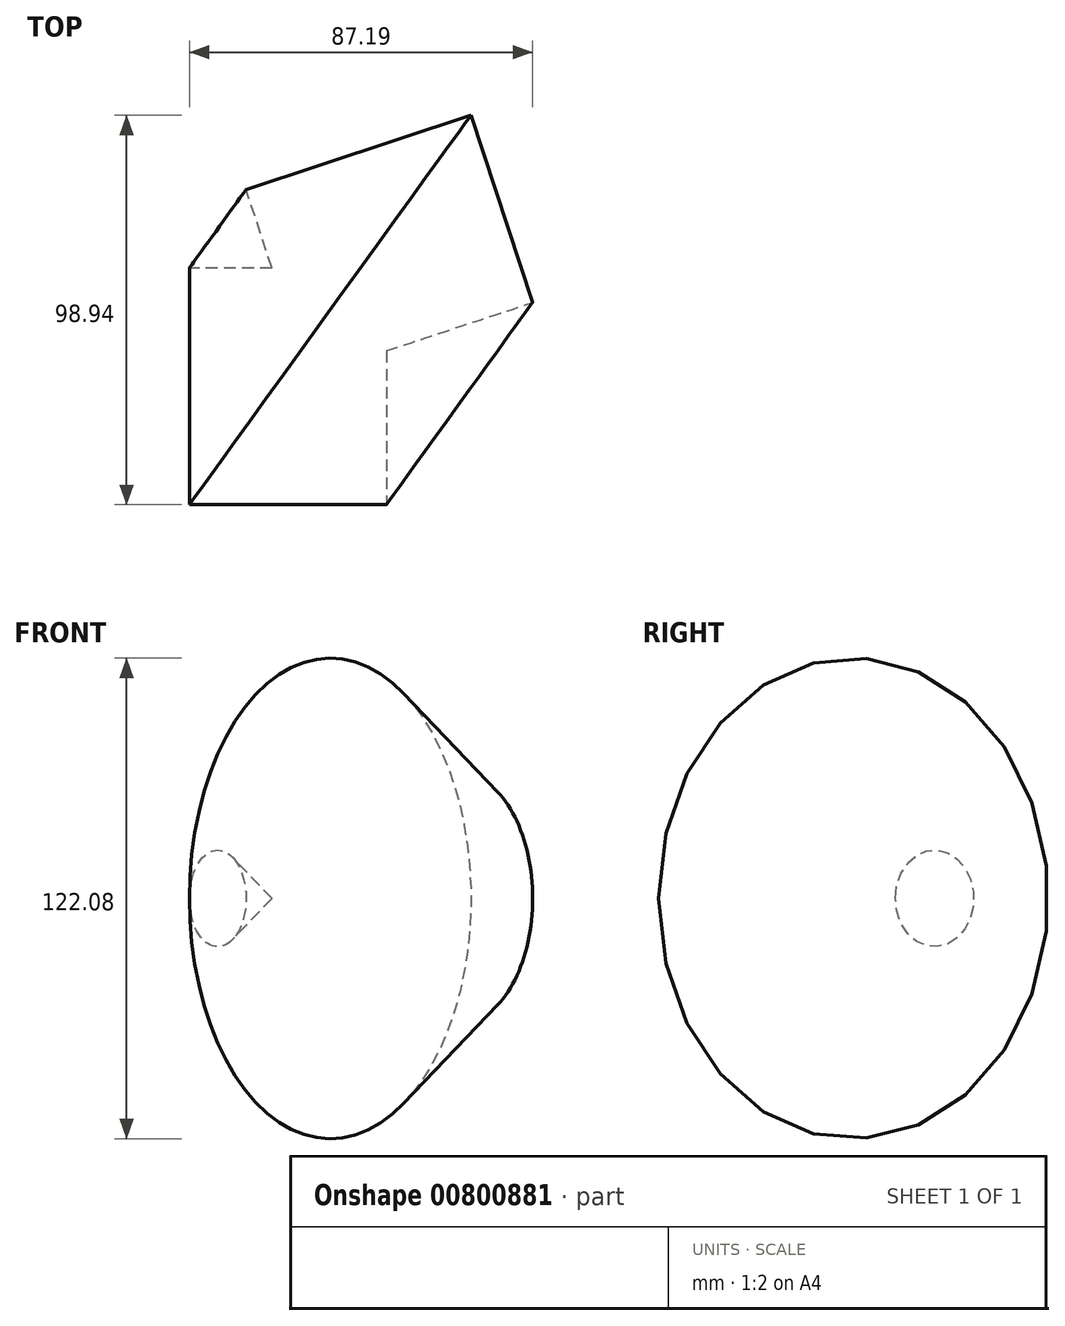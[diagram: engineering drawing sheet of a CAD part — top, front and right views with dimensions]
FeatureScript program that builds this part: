
annotation { "Feature Type Name" : "Feature", "Feature Type Description" : "" }
export const myFeature = defineFeature(function(context is Context, id is Id, definition is map)
    precondition{}
    {
        {
            var Q0;
            Q0=qCreatedBy(makeId("Top.planeOp"),FACE);
            var sketch = newSketch(context, id + "F0", { "sketchPlane" : qUnion([Q0])});
            skLineSegment(sketch, "E0.bottom", {"start": v(-22.75, 24.89) * mm, "end": v(27.33, 24.89) * mm});
            skLineSegment(sketch, "E0.top", {"start": v(-22.75, -35.27) * mm, "end": v(27.33, -35.27) * mm});
            skLineSegment(sketch, "E0.left", {"start": v(-22.75, 24.89) * mm, "end": v(-22.75, -35.27) * mm});
            skLineSegment(sketch, "E0.right", {"start": v(27.33, 24.89) * mm, "end": v(27.33, -35.27) * mm});
            skLineSegment(sketch, "E1", {"start": v(-15.73, 34.97) * mm, "end": v(40.46, -5.65) * mm});
            skSolve(sketch);
        }
        {
            var Q0;
            {var subQ1=sQuery(id+"F0.wireOp",EDGE,"E0.top");Q0=makeQuery(id+"F0.imprint","IMPRINT",FACE,{"disambiguationData":[TD([[makeQuery(id+"F0.imprint","IMPRINT",EDGE,{"derivedFrom":subQ1}),1.0]])]});}
            var Q1;
            Q1=sQuery(id+"F0.wireOp",EDGE,"E1");
            revolve(context, id + "F1", {"surfaceOperationType" : NewSurfaceOperationType.NEW, "entities" : qUnion([Q0]), "axis" : qUnion([Q1]), "revolveType" : RevolveType.FULL});
        }
        {
            var Q0;
            Q0=makeQuery(id+"F1.opRevolve","SWEPT_EDGE",EDGE,{"disambiguationData":[OSD([sQuery(id+"F0.wireOp",EDGE,"E0.top"),sQuery(id+"F0.wireOp",EDGE,"E0.right")])]});
            fillet(context, id + "F2", {"entities" : qUnion([Q0]), "radius" : 0.13 * mm, "tangentPropagation" : true, "allowEdgeOverflow" : false});
        }
    });
